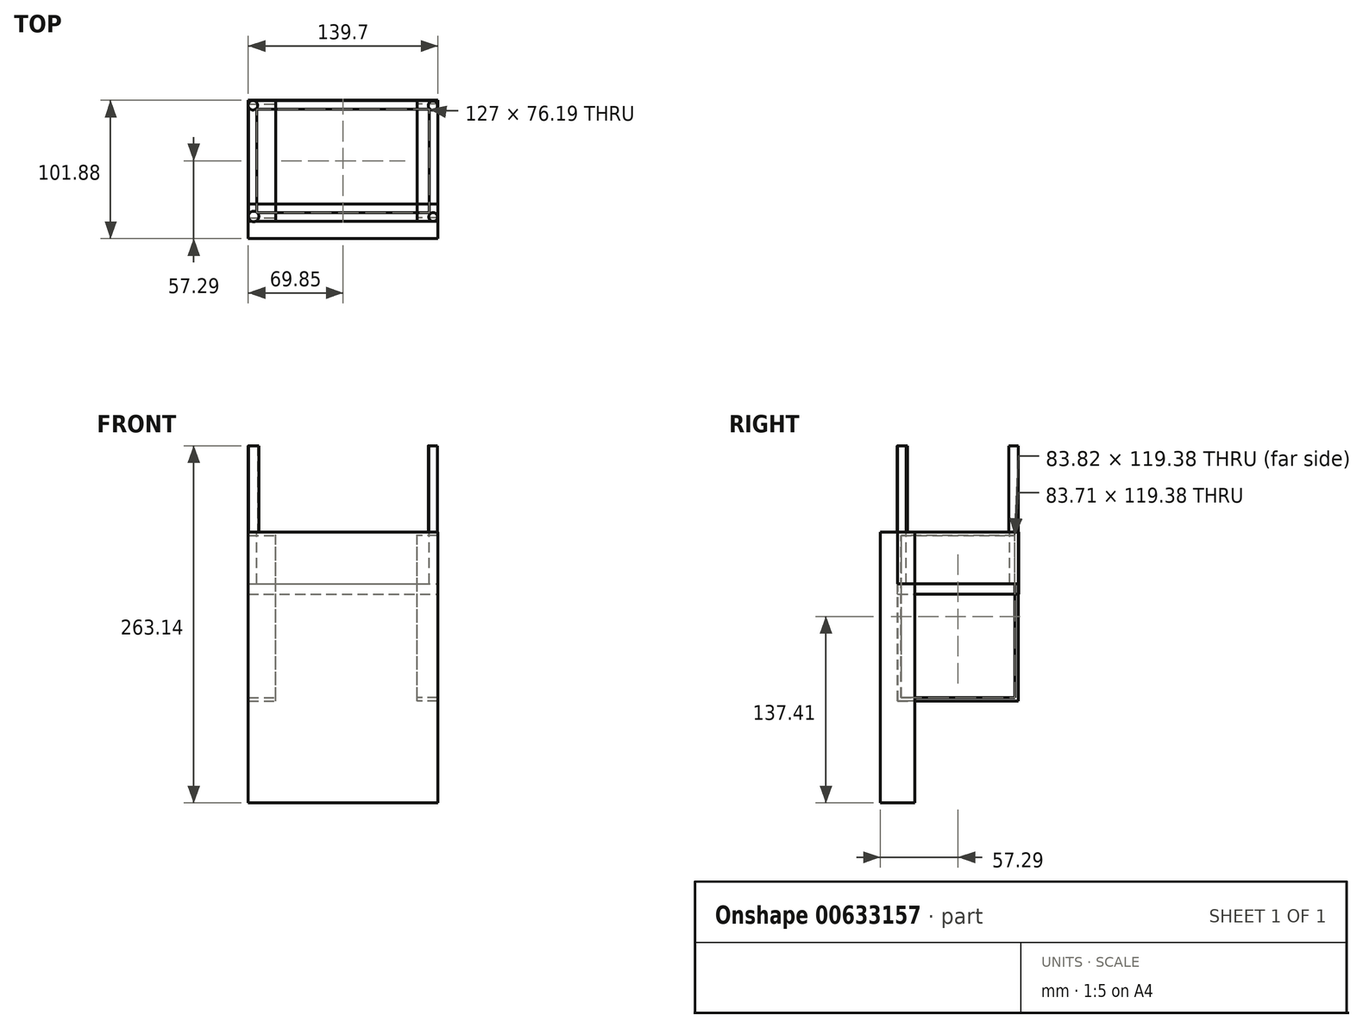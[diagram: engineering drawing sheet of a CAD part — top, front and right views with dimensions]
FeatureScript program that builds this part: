
annotation { "Feature Type Name" : "Feature", "Feature Type Description" : "" }
export const myFeature = defineFeature(function(context is Context, id is Id, definition is map)
    precondition{}
    {
        {
            var Q0;
            Q0=qCreatedBy(makeId("Top.planeOp"),FACE);
            var sketch = newSketch(context, id + "F0", { "sketchPlane" : qUnion([Q0])});
            skLineSegment(sketch, "E0.bottom", {"start": v(-69.85, 44.45) * mm, "end": v(69.85, 44.45) * mm});
            skLineSegment(sketch, "E0.top", {"start": v(-69.85, -44.45) * mm, "end": v(69.85, -44.45) * mm});
            skLineSegment(sketch, "E0.left", {"start": v(-69.85, 44.45) * mm, "end": v(-69.85, -44.45) * mm});
            skLineSegment(sketch, "E0.right", {"start": v(69.85, 44.45) * mm, "end": v(69.85, -44.45) * mm});
            skPoint(sketch, "E0.middle", {"position": v(0, 0) * mm});
            skLineSegment(sketch, "E1.bottom", {"start": v(-63.5, 38.1) * mm, "end": v(63.5, 38.1) * mm});
            skLineSegment(sketch, "E1.top", {"start": v(-63.5, -38.1) * mm, "end": v(63.5, -38.1) * mm});
            skLineSegment(sketch, "E1.left", {"start": v(-63.5, 38.1) * mm, "end": v(-63.5, -38.1) * mm});
            skLineSegment(sketch, "E1.right", {"start": v(63.5, 38.1) * mm, "end": v(63.5, -38.1) * mm});
            skSolve(sketch);
        }
        {
            var Q0;
            Q0=qCreatedBy(makeId("Top.planeOp"),FACE);
            var sketch = newSketch(context, id + "F1", { "sketchPlane" : qUnion([Q0])});
            skCircle(sketch, "E2", {"center": v(-66.36, 40.96) * mm, "radius": 3.46 * mm});
            skCircle(sketch, "E3", {"center": v(66.17, 40.77) * mm, "radius": 3.44 * mm});
            skCircle(sketch, "E4", {"center": v(-65.78, -40.96) * mm, "radius": 3.84 * mm});
            skCircle(sketch, "E5", {"center": v(66.36, -41.34) * mm, "radius": 3.25 * mm});
            skSolve(sketch);
        }
        {
            var Q0;
            Q0 = qSketchRegion(id + "F1", true);
            extrude(context, id + "F2", {"entities" : qUnion([Q0]), "depth" : 63.5 * mm, "offsetDistance" : 25.4 * mm});
        }
        {
            var Q0;
            Q0 = qSketchRegion(id + "F0", true);
            extrude(context, id + "F3", {"entities" : qUnion([Q0]), "oppositeDirection" : true, "depth" : 38.1 * mm, "offsetDistance" : 25.4 * mm});
        }
        {
            var Q0;
            Q0=qCreatedBy(makeId("Top.planeOp"),FACE);
            var sketch = newSketch(context, id + "F4", { "sketchPlane" : qUnion([Q0])});
            skLineSegment(sketch, "E6.bottom", {"start": v(-69.8, -44.59) * mm, "end": v(69.8, -44.59) * mm});
            skLineSegment(sketch, "E6.top", {"start": v(-69.8, 44.59) * mm, "end": v(69.8, 44.59) * mm});
            skLineSegment(sketch, "E6.left", {"start": v(-69.8, -44.59) * mm, "end": v(-69.8, 44.59) * mm});
            skLineSegment(sketch, "E6.right", {"start": v(69.8, -44.59) * mm, "end": v(69.8, 44.59) * mm});
            skPoint(sketch, "E6.middle", {"position": v(0, 0) * mm});
            skSolve(sketch);
        }
        {
            var Q0;
            Q0 = qSketchRegion(id + "F4", true);
            extrude(context, id + "F5", {"entities" : qUnion([Q0]), "oppositeDirection" : true, "depth" : 45.72 * mm, "offsetDistance" : 25.4 * mm});
        }
        {
            var Q0;
            Q0=qCreatedBy(makeId("Top.planeOp"),FACE);
            var sketch = newSketch(context, id + "F6", { "sketchPlane" : qUnion([Q0])});
            skLineSegment(sketch, "E7.bottom", {"start": v(-69.85, -57.29) * mm, "end": v(69.85, -57.29) * mm});
            skLineSegment(sketch, "E7.top", {"start": v(-69.85, -31.89) * mm, "end": v(69.85, -31.89) * mm});
            skLineSegment(sketch, "E7.left", {"start": v(-69.85, -57.29) * mm, "end": v(-69.85, -31.89) * mm});
            skLineSegment(sketch, "E7.right", {"start": v(69.85, -57.29) * mm, "end": v(69.85, -31.89) * mm});
            skPoint(sketch, "E7.middle", {"position": v(0, -44.59) * mm});
            skSolve(sketch);
        }
        {
            var Q0;
            Q0 = qSketchRegion(id + "F6", true);
            extrude(context, id + "F7", {"entities" : qUnion([Q0]), "oppositeDirection" : true, "depth" : 199.64 * mm, "offsetDistance" : 25.4 * mm});
        }
        {
            var Q0;
            Q0=qCreatedBy(makeId("Top.planeOp"),FACE);
            var sketch = newSketch(context, id + "F8", { "sketchPlane" : qUnion([Q0])});
            skLineSegment(sketch, "E8.bottom", {"start": v(-69.7, -44.45) * mm, "end": v(-49.64, -44.45) * mm});
            skLineSegment(sketch, "E8.top", {"start": v(-69.7, 44.45) * mm, "end": v(-49.64, 44.45) * mm});
            skLineSegment(sketch, "E8.left", {"start": v(-69.7, -44.45) * mm, "end": v(-69.7, 44.45) * mm});
            skLineSegment(sketch, "E8.right", {"start": v(-49.64, -44.45) * mm, "end": v(-49.64, 44.45) * mm});
            skPoint(sketch, "E8.middle", {"position": v(-59.67, 0) * mm});
            skLineSegment(sketch, "E9.bottom", {"start": v(69.8, 44.4) * mm, "end": v(54.52, 44.4) * mm});
            skLineSegment(sketch, "E9.top", {"start": v(69.8, -44.4) * mm, "end": v(54.52, -44.4) * mm});
            skLineSegment(sketch, "E9.left", {"start": v(69.8, 44.4) * mm, "end": v(69.8, -44.4) * mm});
            skLineSegment(sketch, "E9.right", {"start": v(54.52, 44.4) * mm, "end": v(54.52, -44.4) * mm});
            skPoint(sketch, "E9.middle", {"position": v(62.16, 0) * mm});
            skSolve(sketch);
        }
        {
            var Q0;
            Q0 = qSketchRegion(id + "F8", true);
            extrude(context, id + "F9", {"entities" : qUnion([Q0]), "oppositeDirection" : true, "depth" : 124.46 * mm, "offsetDistance" : 25.4 * mm});
        }
        {
            var Q0;
            Q0=makeQuery(id+"F9.opExtrude","SWEPT_FACE",FACE,{"disambiguationData":[OSD([sQuery(id+"F8.wireOp",EDGE,"E8.left")])]});
            var Q1;
            Q1=makeQuery(id+"F9.opExtrude","SWEPT_FACE",FACE,{"disambiguationData":[OSD([sQuery(id+"F8.wireOp",EDGE,"E8.right")])]});
            var Q2;
            Q2=makeQuery(id+"F9.opExtrude","SWEPT_FACE",FACE,{"disambiguationData":[OSD([sQuery(id+"F8.wireOp",EDGE,"E9.left")])]});
            var Q3;
            Q3=makeQuery(id+"F9.opExtrude","SWEPT_FACE",FACE,{"disambiguationData":[OSD([sQuery(id+"F8.wireOp",EDGE,"E9.right")])]});
            shell(context, id + "F10", {"entities" : qUnion([Q0, Q1, Q2, Q3]), "thickness" : 2.54 * mm});
        }
    });
